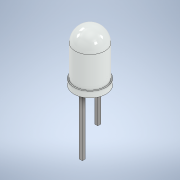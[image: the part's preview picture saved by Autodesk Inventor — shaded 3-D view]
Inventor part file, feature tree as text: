
AUTODESK INVENTOR PART (.ipt)
format: ipt  version: 2022 (Build 260153000, 153)  size: 140,288 bytes
history: native  units: mm
features: sketch x2, other x1, revolve x1, extrude x1
ambient origin geometry x8: Origin, YZ Plane, XZ Plane, XY Plane, X Axis, Y Axis, Z Axis, Center Point
bodies: Body1 (feature_tree)
feature tree (5):
  other  "솔리드1"
  revolve  "회전1"
  extrude  "돌출1"  Depth=2.5mm
  sketch  "스케치1"
  sketch  "스케치2"
